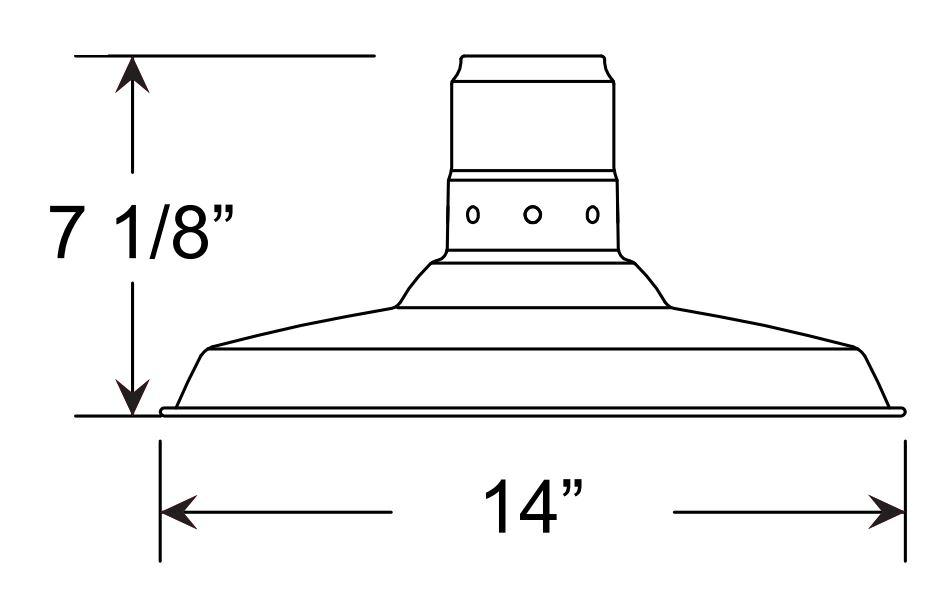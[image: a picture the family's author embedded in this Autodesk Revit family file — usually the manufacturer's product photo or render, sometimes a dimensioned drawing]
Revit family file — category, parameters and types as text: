
# Revit family: OSDC 24,36,42,48 MB
name_source: partatom
category: Lighting Fixtures
units: mm (PartAtom-declared; Revit-internal decimal feet)

## family parameters
Always vertical = Yes
Cut with Voids When Loaded = No
Light Source = Yes
OmniClass Number = 23.80.70.00
OmniClass Title = Lighting
Part Type = Normal
Room Calculation Point = No
Round Connector Dimension = Use Diameter
Shared = No
Work Plane-Based = No

## types (4) — shared parameters
Apparent Load = 200 VA
Body Colour = Spun aluminium
Body Material = body
Bulb = Bulb
CRI = >90
Color Filter = 16777215
Construction Material = Heavy Duty spun aluminum.
Default Elevation = 0' - 0"
Description = 120-277 Voltage
Dimming = 1%
Dimming Lamp Color Temperature Shift = <None>
Efficiency = 65-125 lumens per watt
INSIDE BODY = INSIDE BODY
Lamp = MB
Life = L70 50,000 hours
Load Classification = Lighting
Manufacturer = ANP Lighting
Photometric Web File = OSDC48M037LDDW35K.ies
Power Factor = 1
Tilt Angle = 90.00°
URL = https://www.anplighting.com
Voltage = 277 V
Warranty = 5 year limited warranty
Wattage Comments = 200W Max

## per-type parameters (varying)
| type | Fixture Diameter | Fixture Height | OSDC24 | OSDC36 | OSDC42 | OSDC48 | Weight |
| OSDC24 | 2' - 0" | 0' - 5" | Yes | No | No | No | 8.0 lbs |
| OSDC36 | 3' - 0" | 0' - 6" | No | Yes | No | No | 11.0 lbs |
| OSDC42 | 3' - 6" | 0' - 8" | No | No | Yes | No | 14.5 lbs |
| OSDC48 | 4' - 0" | 0' - 8" | No | No | No | Yes | 18.0 lbs |

note: column(s) folded — value = type name in every type: Model

## geometry (parser evidence)
native form markers: Sweep x70
no freeform markers — native parametric forms only
